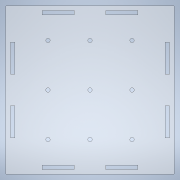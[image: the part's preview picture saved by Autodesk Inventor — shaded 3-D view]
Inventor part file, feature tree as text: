
AUTODESK INVENTOR PART (.ipt)
format: ipt  version: 2021 (Build 250183000, 183)  size: 201,728 bytes
history: native  units: mm
features: sketch x11, hole x9, extrude x2
ambient origin geometry x8: Origin, YZ Plane, XZ Plane, XY Plane, X Axis, Y Axis, Z Axis, Center Point
bodies: Solid1 (feature_tree)
feature tree (22):
  extrude  "Extrusion1"  Depth=106.0mm
  hole  "Hole1"  [1 undecoded]
  sketch  "Sketch3"  dims[d7=1.0mm d8=1.0mm]
  hole  "Hole2"  [1 undecoded]
  hole  "Hole3"  [1 undecoded]
  hole  "Hole4"  [1 undecoded]
  hole  "Hole5"  [1 undecoded]
  hole  "Hole6"  [1 undecoded]
  hole  "Hole7"  [1 undecoded]
  hole  "Hole8"  [1 undecoded]
  hole  "Hole9"  [1 undecoded]
  extrude  "Extrusion2"  Depth=3.0mm
  sketch  "Sketch1"  dims[d0=106.0mm d1=106.0mm]
  sketch  "Sketch2"  dims[d4=3.0mm d5=0.0mm d6=1.0mm]
  sketch  "Sketch5"  dims[d9=1.0mm d10=1.0mm]
  sketch  "Sketch6"  dims[d11=1.0mm d12=1.0mm]
  sketch  "Sketch7"  dims[d13=1.0mm d14=1.0mm]
  sketch  "Sketch8"  dims[d15=3.0mm d16=6.0mm d17=4.0mm d18=2.0mm d19=90.0deg d20=8.0mm d21=20.594885mm d22=3.0mm]
  sketch  "Sketch9"  dims[d23=3.0mm d24=3.0mm]
  sketch  "Sketch10"  dims[d25=3.0mm d26=3.0mm]
  sketch  "Sketch11"  dims[d27=3.0mm d28=3.0mm]
  sketch  "Sketch12"  dims[d29=3.0mm d30=3.0mm d31=6.0mm d32=4.0mm d33=2.0mm d34=90.0deg d35=8.0mm d36=20.594885mm d37=3.0mm d38=3.0mm d39=6.0mm d40=4.0mm d41=2.0mm d42=90.0deg d43=8.0mm d44=20.594885mm d45=3.0mm d46=3.0mm d47=6.0mm d48=4.0mm d49=2.0mm d50=90.0deg d51=8.0mm d52=20.594885mm d53=3.0mm d54=3.0mm d55=6.0mm d56=4.0mm d57=2.0mm d58=90.0deg d59=8.0mm d60=20.594885mm d61=3.0mm d62=3.0mm d63=6.0mm d64=4.0mm d65=2.0mm d66=90.0deg d67=8.0mm d68=20.594885mm d69=3.0mm d70=3.0mm d71=6.0mm d72=4.0mm d73=2.0mm d74=90.0deg d75=8.0mm d76=20.594885mm d77=3.0mm d78=3.0mm d79=6.0mm d80=4.0mm d81=2.0mm d82=90.0deg d83=8.0mm d84=20.594885mm d85=3.0mm d86=3.0mm d87=6.0mm d88=4.0mm d89=2.0mm d90=90.0deg d91=8.0mm d92=20.594885mm d99=112.0mm d100=112.0mm d101=3.0mm d102=0.0mm d103=0.5mm d104=0.872665mm]
note: 9 required parameter values undecoded (feature->parameter linkage not recoverable at this tier; creation-order binding heuristic only, values carry confidence <= 0.55)
